# Revit family: AHD-D
name_source: partatom
category: Lighting Fixtures
revit_build: Autodesk Revit 2014 (Build: 20130308_1515(x64)
units: mm (PartAtom-declared; Revit-internal decimal feet)

## types (2) — shared parameters
Apparent Load = 7 VA
Certification = UL924 Damp Listed, NFPA 101 and NFPA 70
Default Elevation = 48 "
Description = Stamped alumiunum housing with metal swivel.
Features = Style matches AS emergency lighting unit
Available in white or black finishes
Supplied with rectangular mounting plate
Glass = Glass - Hubbell - White
Lamp = Incandescent, Halogen PAR 36 Lamp
Manufacturer = Dual-Lite Lighting A unit of Hubbell Lighting
Model = AHD
Product Doucumentation Link = https://hubbellcdn.com
Product Page URL = https://www.hubbell.com
Steel = Metal-Hubbell-Galvanized_Steel
Type Comments = Light Fixture
URL = https://www.hubbell.com
Warranty = Please refer to the Warranty Link
Warranty Notes = https://hubbellcdn.com
Wattage Comments = 7W

## per-type parameters (varying)
| type | Body |
| AHD-D-W | Paint - Hubbell - Matte White |
| AHD-D-B | Paint - Hubbell - Black Matte Textured |

## geometry (parser evidence)
native form markers: Sweep x1
no freeform markers — native parametric forms only
